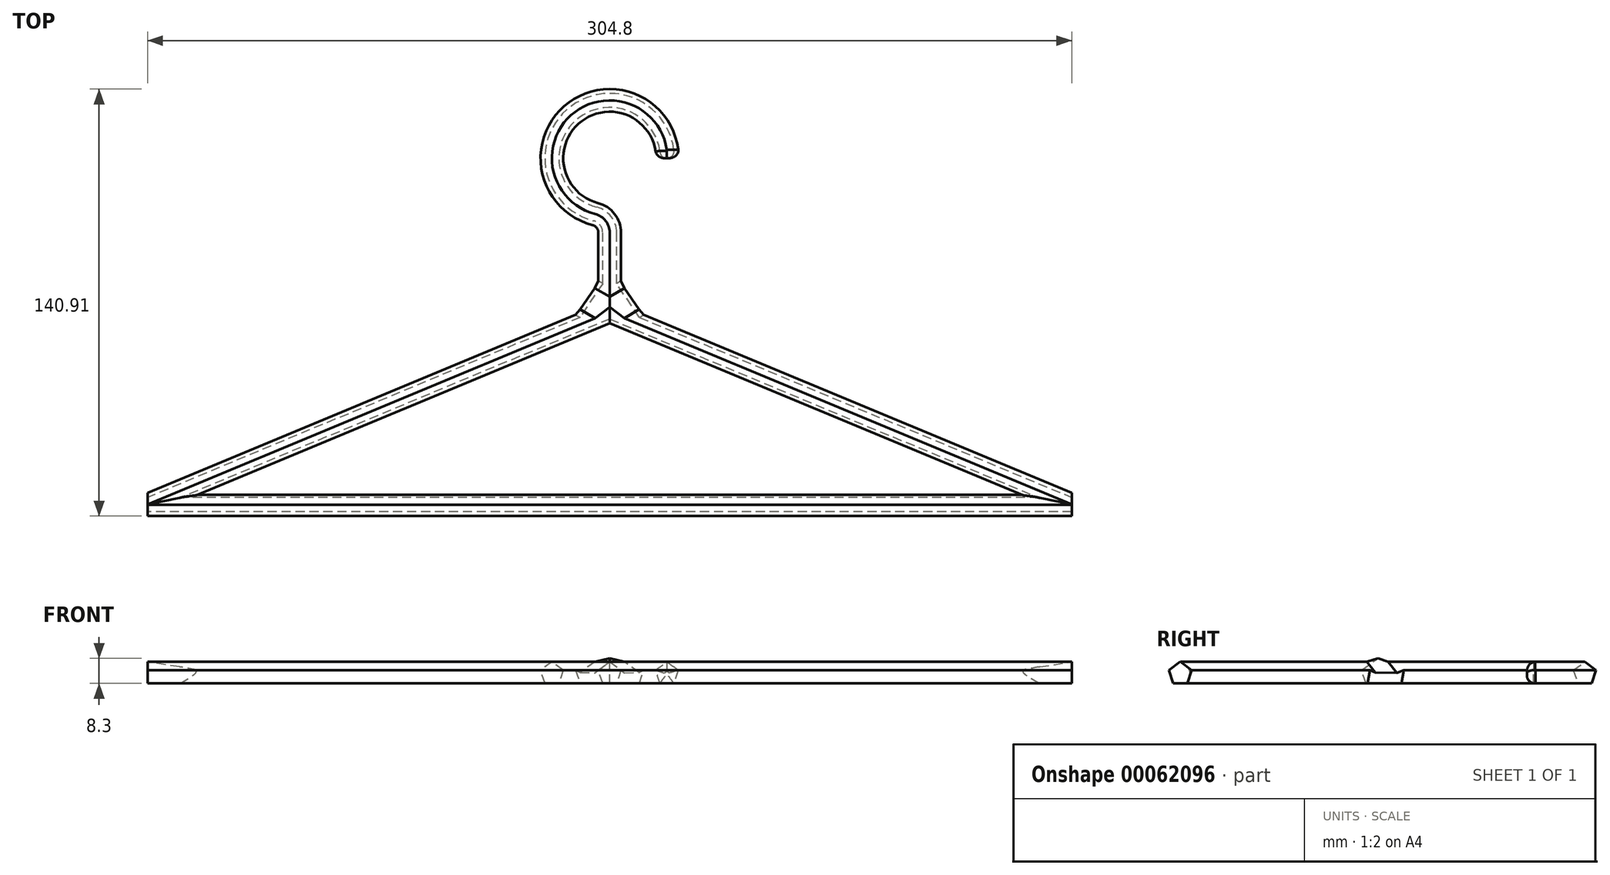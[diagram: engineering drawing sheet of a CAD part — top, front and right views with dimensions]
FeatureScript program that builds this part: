
annotation { "Feature Type Name" : "Feature", "Feature Type Description" : "" }
export const myFeature = defineFeature(function(context is Context, id is Id, definition is map)
    precondition{}
    {
        {
            var Q0;
            Q0=qCreatedBy(makeId("Top.planeOp"),FACE);
            var sketch = newSketch(context, id + "F0", { "sketchPlane" : qUnion([Q0])});
            skLineSegment(sketch, "E0", {"start": v(0, 0) * mm, "end": v(0, 26.2) * mm});
            skArc(sketch, "E1", {"start": v(19.05, 50.8) * mm, "mid": v(-11.67, 65.86) * mm, "end": v(-4.76, 32.35) * mm});
            skLineSegment(sketch, "E2", {"start": v(-152.4, 68.06) * mm, "end": v(-152.4, -63.5) * mm, "construction": true});
            skPoint(sketch, "E3.visualSharp", {"position": v(0, 31.75) * mm});
            skArc(sketch, "E3.filletArc", {"start": v(0, 26.2) * mm, "mid": v(-1.33, 30.1) * mm, "end": v(-4.76, 32.35) * mm});
            skLineSegment(sketch, "E4", {"start": v(0, 0) * mm, "end": v(-152.4, -63.5) * mm});
            skLineSegment(sketch, "E5", {"start": v(-152.4, -63.5) * mm, "end": v(0, -63.5) * mm});
            skSolve(sketch);
        }
        {
            var Q0;
            Q0=qCreatedBy(makeId("Right.planeOp"),FACE);
            var sketch = newSketch(context, id + "F1", { "sketchPlane" : qUnion([Q0])});
            skCircle(sketch, "E6.cCircle", {"center": v(0, 0) * mm, "radius": 3.18 * mm, "construction": true});
            skLineSegment(sketch, "E6.0", {"start": v(2.3, -3.17) * mm, "end": v(-2.3, -3.17) * mm});
            skLineSegment(sketch, "E6.1", {"start": v(-2.3, -3.17) * mm, "end": v(-3.73, 1.21) * mm});
            skLineSegment(sketch, "E6.2", {"start": v(-3.73, 1.21) * mm, "end": v(0, 3.92) * mm});
            skLineSegment(sketch, "E6.3", {"start": v(0, 3.92) * mm, "end": v(3.73, 1.21) * mm});
            skLineSegment(sketch, "E6.4", {"start": v(3.73, 1.21) * mm, "end": v(2.3, -3.17) * mm});
            skPoint(sketch, "E6.0.midPoint", {"position": v(0, -3.18) * mm});
            skCircle(sketch, "E7.cCircle", {"center": v(-63.6, 0) * mm, "radius": 3.18 * mm, "construction": true});
            skLineSegment(sketch, "E7.0", {"start": v(-61.3, -3.18) * mm, "end": v(-65.9, -3.18) * mm});
            skLineSegment(sketch, "E7.1", {"start": v(-65.9, -3.17) * mm, "end": v(-67.33, 1.21) * mm});
            skLineSegment(sketch, "E7.2", {"start": v(-67.33, 1.21) * mm, "end": v(-63.6, 3.92) * mm});
            skLineSegment(sketch, "E7.3", {"start": v(-63.6, 3.92) * mm, "end": v(-59.86, 1.21) * mm});
            skLineSegment(sketch, "E7.4", {"start": v(-59.86, 1.21) * mm, "end": v(-61.3, -3.17) * mm});
            skPoint(sketch, "E7.0.midPoint", {"position": v(-63.6, -3.18) * mm});
            skSolve(sketch);
        }
        {
            var Q0;
            Q0=makeQuery(id+"F1.imprint","IMPRINT",FACE,{"disambiguationData":[TD([[makeQuery(id+"F1.imprint","IMPRINT",EDGE,{"derivedFrom":sQuery(id+"F1.wireOp",EDGE,"E6.0")}),-1.0]])]});
            var Q1;
            Q1=sQuery(id+"F0.wireOp",EDGE,"E4");
            sweep(context, id + "F2", {"profiles" : qUnion([Q0]), "path" : qUnion([Q1]), "keepProfileOrientation" : true});
        }
        {
            var Q0;
            Q0=qCreatedBy(makeId("Front.planeOp"),FACE);
            var sketch = newSketch(context, id + "F3", { "sketchPlane" : qUnion([Q0])});
            skCircle(sketch, "E8.cCircle", {"center": v(0, 0) * mm, "radius": 3.18 * mm, "construction": true});
            skLineSegment(sketch, "E8.0", {"start": v(2.3, -3.17) * mm, "end": v(-2.3, -3.17) * mm});
            skLineSegment(sketch, "E8.1", {"start": v(-2.3, -3.17) * mm, "end": v(-3.73, 1.21) * mm});
            skLineSegment(sketch, "E8.2", {"start": v(-3.73, 1.21) * mm, "end": v(0, 3.92) * mm});
            skLineSegment(sketch, "E8.3", {"start": v(0, 3.92) * mm, "end": v(3.73, 1.21) * mm});
            skLineSegment(sketch, "E8.4", {"start": v(3.73, 1.21) * mm, "end": v(2.3, -3.17) * mm});
            skPoint(sketch, "E8.0.midPoint", {"position": v(0, -3.18) * mm});
            skSolve(sketch);
        }
        {
            var Q0;
            Q0=makeQuery(id+"F3.imprint","IMPRINT",FACE,{"disambiguationData":[TD([[makeQuery(id+"F3.imprint","IMPRINT",EDGE,{"derivedFrom":sQuery(id+"F3.wireOp",EDGE,"E8.0")}),-1.0]])]});
            var Q1;
            Q1=sQuery(id+"F0.wireOp",EDGE,"E3.filletArc");
            var Q2;
            Q2=sQuery(id+"F0.wireOp",EDGE,"E1");
            var Q3;
            Q3=sQuery(id+"F0.wireOp",EDGE,"E0");
            sweep(context, id + "F4", {"profiles" : qUnion([Q0]), "path" : qUnion([Q1, Q2, Q3])});
        }
        {
            var Q0;
            Q0=makeQuery(id+"F1.imprint","IMPRINT",FACE,{"disambiguationData":[TD([[makeQuery(id+"F1.imprint","IMPRINT",EDGE,{"derivedFrom":sQuery(id+"F1.wireOp",EDGE,"E7.0")}),-1.0]])]});
            var Q1;
            Q1=sQuery(id+"F0.wireOp",EDGE,"E5");
            sweep(context, id + "F5", {"operationType" : NewBodyOperationType.ADD, "profiles" : qUnion([Q0]), "path" : qUnion([Q1])});
        }
        {
            var Q0;
            Q0=makeQuery(id+"F2.opSweep","SWEPT_BODY",BODY,{"disambiguationData":[OSD([sQuery(id+"F0.wireOp",EDGE,"E4"),sQuery(id+"F1.wireOp",EDGE,"E6.0"),sQuery(id+"F1.wireOp",EDGE,"E6.1"),sQuery(id+"F1.wireOp",EDGE,"E6.2"),sQuery(id+"F1.wireOp",EDGE,"E6.3"),sQuery(id+"F1.wireOp",EDGE,"E6.4")])]});
            var Q1;
            Q1=qCreatedBy(makeId("Right.planeOp"),FACE);
            mirror(context, id + "F6", {"entities" : qUnion([Q0]), "mirrorPlane" : qUnion([Q1])});
        }
        {
            var Q0;
            Q0=makeQuery(id+"F4.opSweep","SWEPT_BODY",BODY,{"disambiguationData":[OSD([sQuery(id+"F0.wireOp",EDGE,"E0"),sQuery(id+"F3.wireOp",EDGE,"E8.0"),sQuery(id+"F3.wireOp",EDGE,"E8.1"),sQuery(id+"F3.wireOp",EDGE,"E8.2"),sQuery(id+"F3.wireOp",EDGE,"E8.3"),sQuery(id+"F3.wireOp",EDGE,"E8.4")])]});
            var Q1;
            Q1=makeQuery(id+"F2.opSweep","SWEPT_BODY",BODY,{"disambiguationData":[OSD([sQuery(id+"F0.wireOp",EDGE,"E4"),sQuery(id+"F1.wireOp",EDGE,"E6.0"),sQuery(id+"F1.wireOp",EDGE,"E6.1"),sQuery(id+"F1.wireOp",EDGE,"E6.2"),sQuery(id+"F1.wireOp",EDGE,"E6.3"),sQuery(id+"F1.wireOp",EDGE,"E6.4")])]});
            var Q2;
            Q2=makeQuery(id+"F6.opPattern","COPY",BODY,{"derivedFrom":makeQuery(id+"F2.opSweep","SWEPT_BODY",BODY,{"disambiguationData":[OSD([sQuery(id+"F0.wireOp",EDGE,"E4"),sQuery(id+"F1.wireOp",EDGE,"E6.0"),sQuery(id+"F1.wireOp",EDGE,"E6.1"),sQuery(id+"F1.wireOp",EDGE,"E6.2"),sQuery(id+"F1.wireOp",EDGE,"E6.3"),sQuery(id+"F1.wireOp",EDGE,"E6.4")])]}),"instanceName":"1"});
            booleanBodies(context, id + "F7", {"operationType" : BooleanOperationType.UNION, "tools" : qUnion([Q0, Q1, Q2]), "keepTools" : true});
        }
        {
            var Q0;
            Q0=makeQuery(id+"F4.opSweep","CAP_EDGE",EDGE,{"disambiguationData":[OSD([sQuery(id+"F0.wireOp",VERTEX,"E1.start"),sQuery(id+"F3.wireOp",EDGE,"079b0d4f-e7cb-407d-a380-d36e278eac54")])],"isStart":false});
            fillet(context, id + "F8", {"entities" : qUnion([Q0]), "radius" : 2.54 * mm, "tangentPropagation" : true, "allowEdgeOverflow" : false});
        }
        {
            var Q0;
            Q0=makeQuery(id+"F7.opBoolean","INTERSECT",EDGE,{"derivedFrom":[makeQuery(id+"F2.opSweep","SWEPT_FACE",FACE,{"disambiguationData":[OSD([sQuery(id+"F0.wireOp",EDGE,"E4"),sQuery(id+"F1.wireOp",EDGE,"E6.3")])]}),makeQuery(id+"F4.opSweep","SWEPT_FACE",FACE,{"disambiguationData":[OSD([sQuery(id+"F0.wireOp",EDGE,"E0"),sQuery(id+"F3.wireOp",EDGE,"E8.2")])]})]});
            var Q1;
            Q1=makeQuery(id+"F7.opBoolean","INTERSECT",EDGE,{"derivedFrom":[makeQuery(id+"F2.opSweep","SWEPT_FACE",FACE,{"disambiguationData":[OSD([sQuery(id+"F0.wireOp",EDGE,"E4"),sQuery(id+"F1.wireOp",EDGE,"E6.4")])]}),makeQuery(id+"F4.opSweep","SWEPT_FACE",FACE,{"disambiguationData":[OSD([sQuery(id+"F0.wireOp",EDGE,"E0"),sQuery(id+"F3.wireOp",EDGE,"E8.1")])]})]});
            chamfer(context, id + "F9", {"entities" : qUnion([Q0, Q1]), "width" : 12.7 * mm, "tangentPropagation" : true});
        }
        {
            var Q0;
            Q0=makeQuery(id+"F7.opBoolean","INTERSECT",EDGE,{"derivedFrom":[makeQuery(id+"F4.opSweep","SWEPT_FACE",FACE,{"disambiguationData":[OSD([sQuery(id+"F0.wireOp",EDGE,"E0"),sQuery(id+"F3.wireOp",EDGE,"E8.3")])]}),makeQuery(id+"F6.opPattern","COPY",FACE,{"derivedFrom":makeQuery(id+"F2.opSweep","SWEPT_FACE",FACE,{"disambiguationData":[OSD([sQuery(id+"F0.wireOp",EDGE,"E4"),sQuery(id+"F1.wireOp",EDGE,"E6.3")])]}),"instanceName":"1"})]});
            var Q1;
            Q1=makeQuery(id+"F7.opBoolean","INTERSECT",EDGE,{"derivedFrom":[makeQuery(id+"F4.opSweep","SWEPT_FACE",FACE,{"disambiguationData":[OSD([sQuery(id+"F0.wireOp",EDGE,"E0"),sQuery(id+"F3.wireOp",EDGE,"E8.4")])]}),makeQuery(id+"F6.opPattern","COPY",FACE,{"derivedFrom":makeQuery(id+"F2.opSweep","SWEPT_FACE",FACE,{"disambiguationData":[OSD([sQuery(id+"F0.wireOp",EDGE,"E4"),sQuery(id+"F1.wireOp",EDGE,"E6.4")])]}),"instanceName":"1"})]});
            chamfer(context, id + "F10", {"entities" : qUnion([Q0, Q1]), "width" : 12.7 * mm, "tangentPropagation" : true});
        }
        {
            var Q0;
            {var subQ0=makeQuery(id+"F5.opSweep","SWEPT_EDGE",EDGE,{"disambiguationData":[OSD([sQuery(id+"F0.wireOp",EDGE,"E5"),sQuery(id+"F1.wireOp",EDGE,"E7.3"),sQuery(id+"F1.wireOp",EDGE,"E7.4")])]});Q0=makeQuery(id+"F7.opBoolean","MERGE",EDGE,{"derivedFrom":[subQ0,makeQuery(id+"F6.opPattern","COPY",EDGE,{"derivedFrom":subQ0,"instanceName":"1"})]});}
            fillet(context, id + "F11", {"entities" : qUnion([Q0]), "radius" : 2.54 * mm, "tangentPropagation" : true, "allowEdgeOverflow" : false});
        }
    });
